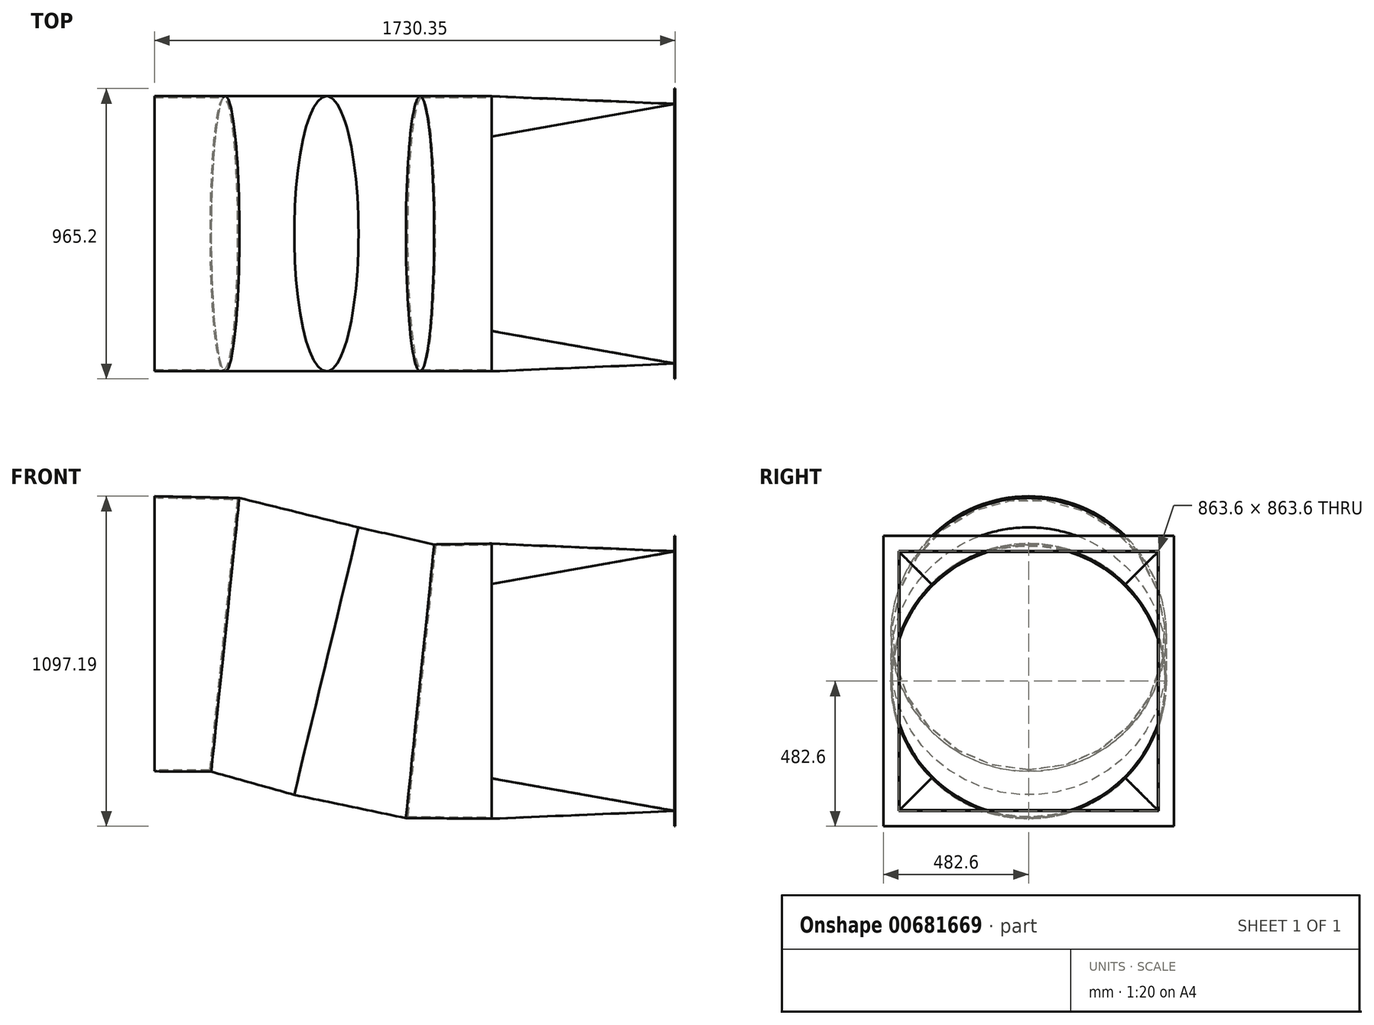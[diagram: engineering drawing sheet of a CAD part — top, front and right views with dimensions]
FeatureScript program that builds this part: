
annotation { "Feature Type Name" : "Feature", "Feature Type Description" : "" }
export const myFeature = defineFeature(function(context is Context, id is Id, definition is map)
    precondition{}
    {
        {
            var Q0;
            Q0=qCreatedBy(makeId("Right.planeOp"),FACE);
            var sketch = newSketch(context, id + "F0", { "sketchPlane" : qUnion([Q0])});
            skLineSegment(sketch, "E0.bottom", {"start": v(482.6, 482.6) * mm, "end": v(-482.6, 482.6) * mm});
            skLineSegment(sketch, "E0.top", {"start": v(482.6, -482.6) * mm, "end": v(-482.6, -482.6) * mm});
            skLineSegment(sketch, "E0.left", {"start": v(482.6, 482.6) * mm, "end": v(482.6, -482.6) * mm});
            skLineSegment(sketch, "E0.right", {"start": v(-482.6, 482.6) * mm, "end": v(-482.6, -482.6) * mm});
            skPoint(sketch, "E0.middle", {"position": v(0, 0) * mm});
            skCircle(sketch, "E1", {"center": v(0, 0) * mm, "radius": 431.8 * mm});
            skLineSegment(sketch, "E2.bottom", {"start": v(431.8, 431.8) * mm, "end": v(-431.8, 431.8) * mm});
            skLineSegment(sketch, "E2.top", {"start": v(431.8, -431.8) * mm, "end": v(-431.8, -431.8) * mm});
            skLineSegment(sketch, "E2.left", {"start": v(431.8, 431.8) * mm, "end": v(431.8, -431.8) * mm});
            skLineSegment(sketch, "E2.right", {"start": v(-431.8, 431.8) * mm, "end": v(-431.8, -431.8) * mm});
            skSolve(sketch);
        }
        {
            var Q0;
            Q0=makeQuery(id+"F0.imprint","IMPRINT",FACE,{"disambiguationData":[TD([[makeQuery(id+"F0.imprint","IMPRINT",EDGE,{"derivedFrom":sQuery(id+"F0.wireOp",EDGE,"E0.bottom")}),1.0]])]});
            extrude(context, id + "F1", {"entities" : qUnion([Q0]), "oppositeDirection" : true, "depth" : 3.17 * mm, "offsetDistance" : 25.4 * mm});
        }
        {
            var Q0;
            {var subQ0=sQuery(id+"F0.wireOp",EDGE,"E1");var subQ1=makeQuery(id+"F0.imprint","INTERSECT",VERTEX,{"derivedFrom":[subQ0,sQuery(id+"F0.wireOp",EDGE,"E2.bottom")]});Q0=makeQuery(id+"F0.imprint","IMPRINT",FACE,{"disambiguationData":[TD([[makeQuery(id+"F0.imprint","IMPRINT",EDGE,{"disambiguationData":[TD([[subQ1,1.0]])],"derivedFrom":subQ0}),1.0]])]});}
            cPlane(context, id + "F2", {"entities" : qUnion([Q0]), "cplaneType" : CPlaneType.OFFSET, "offset" : 609.6 * mm, "oppositeDirection" : true, "width" : 152.4 * mm, "height" : 152.4 * mm});
        }
        {
            var Q0;
            Q0=qCreatedBy(id+"F2.planeOp",FACE);
            var sketch = newSketch(context, id + "F3", { "sketchPlane" : qUnion([Q0])});
            skCircle(sketch, "E3", {"center": v(0, 0) * mm, "radius": 457.2 * mm});
            skSolve(sketch);
        }
        {
            var Q0;
            Q0=qCreatedBy(makeId("Right.planeOp"),FACE);
            var sketch = newSketch(context, id + "F4", { "sketchPlane" : qUnion([Q0])});
            skLineSegment(sketch, "E4.bottom", {"start": v(431.8, 431.8) * mm, "end": v(-431.8, 431.8) * mm});
            skLineSegment(sketch, "E4.top", {"start": v(431.8, -431.8) * mm, "end": v(-431.8, -431.8) * mm});
            skLineSegment(sketch, "E4.left", {"start": v(431.8, 431.8) * mm, "end": v(431.8, -431.8) * mm});
            skLineSegment(sketch, "E4.right", {"start": v(-431.8, 431.8) * mm, "end": v(-431.8, -431.8) * mm});
            skSolve(sketch);
        }
        {
            var Q1;
            Q1=makeQuery(id+"F3.imprint","IMPRINT",FACE,{"disambiguationData":[TD([[makeQuery(id+"F3.imprint","IMPRINT",EDGE,{"derivedFrom":sQuery(id+"F3.wireOp",EDGE,"E3")}),1.0]])]});
            var Q2;
            Q2=makeQuery(id+"F4.imprint","IMPRINT",FACE,{"disambiguationData":[TD([[makeQuery(id+"F4.imprint","IMPRINT",EDGE,{"derivedFrom":sQuery(id+"F4.wireOp",EDGE,"E4.bottom")}),1.0]])]});
            loft(context, id + "F5", {"sheetProfilesArray" : [{ "sheetProfileEntities" : qUnion([Q1]) }, { "sheetProfileEntities" : qUnion([Q2]) }]});
        }
        {
            var Q0;
            Q0=makeQuery(id+"F5.opLoft","CAP_FACE",FACE,{"disambiguationData":[OSD([makeQuery(id+"F3.imprint","IMPRINT",FACE,{"disambiguationData":[TD([[makeQuery(id+"F3.imprint","IMPRINT",EDGE,{"derivedFrom":sQuery(id+"F3.wireOp",EDGE,"E3")}),1.0]])]})])],"isStart":true});
            var Q1;
            Q1=makeQuery(id+"F5.opLoft","CAP_FACE",FACE,{"disambiguationData":[OSD([makeQuery(id+"F4.imprint","IMPRINT",FACE,{"disambiguationData":[TD([[makeQuery(id+"F4.imprint","IMPRINT",EDGE,{"derivedFrom":sQuery(id+"F4.wireOp",EDGE,"E4.bottom")}),1.0]])]})])],"isStart":true});
            shell(context, id + "F6", {"entities" : qUnion([Q0, Q1]), "thickness" : 2.54 * mm});
        }
        {
            var Q0;
            Q0=qCreatedBy(makeId("Front.planeOp"),FACE);
            var sketch = newSketch(context, id + "F7", { "sketchPlane" : qUnion([Q0])});
            skLineSegment(sketch, "E5", {"start": v(-611.03, 0) * mm, "end": v(-2931.64, 0) * mm, "construction": true});
            skLineSegment(sketch, "E6.bottom", {"start": v(-612.75, 435.19) * mm, "end": v(-1730.35, 435.19) * mm});
            skLineSegment(sketch, "E6.top", {"start": v(-612.75, -428.41) * mm, "end": v(-1730.35, -428.41) * mm});
            skLineSegment(sketch, "E6.left", {"start": v(-612.75, 435.19) * mm, "end": v(-612.75, -428.41) * mm});
            skLineSegment(sketch, "E6.right", {"start": v(-1730.35, 435.19) * mm, "end": v(-1730.35, -428.41) * mm});
            skLineSegment(sketch, "E7.bottom", {"start": v(-612.75, 435.19) * mm, "end": v(-1729.64, 435.19) * mm});
            skLineSegment(sketch, "E7.top", {"start": v(-612.75, 590.76) * mm, "end": v(-1729.64, 590.76) * mm});
            skLineSegment(sketch, "E7.left", {"start": v(-612.75, 435.19) * mm, "end": v(-612.75, 590.76) * mm});
            skLineSegment(sketch, "E7.right", {"start": v(-1729.64, 435.19) * mm, "end": v(-1729.64, 590.76) * mm});
            skLineSegment(sketch, "E8.bottom", {"start": v(-612.75, 435.19) * mm, "end": v(-803.25, 435.19) * mm});
            skLineSegment(sketch, "E8.top", {"start": v(-612.75, -428.41) * mm, "end": v(-803.25, -428.41) * mm});
            skLineSegment(sketch, "E9.bottom", {"start": v(-1729.64, 590.76) * mm, "end": v(-1450.24, 590.76) * mm});
            skLineSegment(sketch, "E9.top", {"start": v(-1729.64, -272.84) * mm, "end": v(-1539.14, -272.84) * mm});
            skLineSegment(sketch, "E9.left", {"start": v(-1729.64, 590.76) * mm, "end": v(-1729.64, -272.84) * mm});
            skLineSegment(sketch, "E10", {"start": v(-803.25, 435.19) * mm, "end": v(-1450.24, 590.76) * mm});
            skLineSegment(sketch, "E11.bottom", {"start": v(-612.75, -428.41) * mm, "end": v(-892.15, -428.41) * mm});
            skLineSegment(sketch, "E11.left", {"start": v(-612.75, -428.41) * mm, "end": v(-612.75, -156.4) * mm});
            skLineSegment(sketch, "E12.left", {"start": v(-1729.64, -272.84) * mm, "end": v(-1729.64, -35.15) * mm});
            skLineSegment(sketch, "E13", {"start": v(-892.15, -428.41) * mm, "end": v(-1539.14, -272.84) * mm});
            skLineSegment(sketch, "E14.bottom", {"start": v(-1450.24, 590.76) * mm, "end": v(-1056.12, 590.76) * mm});
            skLineSegment(sketch, "E15", {"start": v(-1056.12, 495.99) * mm, "end": v(-1257.29, -340.61) * mm});
            skLineSegment(sketch, "E16", {"start": v(-1450.24, 590.76) * mm, "end": v(-1539.14, -272.84) * mm});
            skLineSegment(sketch, "E17", {"start": v(-803.25, 435.19) * mm, "end": v(-892.15, -428.41) * mm});
            skLineSegment(sketch, "E18", {"start": v(-848.05, 0) * mm, "end": v(-1156.7, 77.69) * mm, "construction": true});
            skLineSegment(sketch, "E19", {"start": v(-1156.7, 77.69) * mm, "end": v(-1494.7, 158.96) * mm, "construction": true});
            skLineSegment(sketch, "E20", {"start": v(-1494.7, 158.96) * mm, "end": v(-1730.35, 158.96) * mm, "construction": true});
            skSolve(sketch);
        }
        {
            var Q0;
            Q0=sQuery(id+"F7.wireOp",EDGE,"E17");
            cPlane(context, id + "F8", {"entities" : qUnion([Q0]), "cplaneType" : CPlaneType.LINE_ANGLE, "offset" : 25.4 * mm, "angle" : 0 * degree, "width" : 152.4 * mm, "height" : 152.4 * mm});
        }
        {
            var Q0;
            Q0=sQuery(id+"F7.wireOp",EDGE,"E15");
            cPlane(context, id + "F9", {"entities" : qUnion([Q0]), "cplaneType" : CPlaneType.LINE_ANGLE, "offset" : 25.4 * mm, "angle" : 0 * degree, "width" : 152.4 * mm, "height" : 152.4 * mm});
        }
        {
            var Q0;
            Q0=sQuery(id+"F7.wireOp",EDGE,"E16");
            cPlane(context, id + "F10", {"entities" : qUnion([Q0]), "cplaneType" : CPlaneType.LINE_ANGLE, "offset" : 25.4 * mm, "angle" : 0 * degree, "width" : 152.4 * mm, "height" : 152.4 * mm});
        }
        {
            var Q0;
            Q0=sQuery(id+"F7.wireOp",EDGE,"E6.right");
            cPlane(context, id + "F11", {"entities" : qUnion([Q0]), "cplaneType" : CPlaneType.LINE_ANGLE, "offset" : 25.4 * mm, "angle" : 0 * degree, "width" : 152.4 * mm, "height" : 152.4 * mm});
        }
        {
            var Q0;
            Q0=qCreatedBy(id+"F9.planeOp",FACE);
            var sketch = newSketch(context, id + "F12", { "sketchPlane" : qUnion([Q0])});
            skCircle(sketch, "E21", {"center": v(0, -206.28) * mm, "radius": 457.2 * mm});
            skSolve(sketch);
        }
        {
            var Q0;
            Q0=qCreatedBy(id+"F10.planeOp",FACE);
            var sketch = newSketch(context, id + "F13", { "sketchPlane" : qUnion([Q0])});
            skCircle(sketch, "E22", {"center": v(0, 0) * mm, "radius": 457.2 * mm});
            skSolve(sketch);
        }
        {
            var Q0;
            Q0=qCreatedBy(id+"F8.planeOp",FACE);
            var sketch = newSketch(context, id + "F14", { "sketchPlane" : qUnion([Q0])});
            skCircle(sketch, "E23", {"center": v(0, -87.24) * mm, "radius": 457.2 * mm});
            skSolve(sketch);
        }
        {
            var Q0;
            Q0=qCreatedBy(id+"F2.planeOp",FACE);
            var sketch = newSketch(context, id + "F15", { "sketchPlane" : qUnion([Q0])});
            skCircle(sketch, "E24", {"center": v(0, 0) * mm, "radius": 457.2 * mm});
            skSolve(sketch);
        }
        {
            var Q0;
            Q0=makeQuery(id+"F15.imprint","IMPRINT",FACE,{"disambiguationData":[TD([[makeQuery(id+"F15.imprint","IMPRINT",EDGE,{"derivedFrom":sQuery(id+"F15.wireOp",EDGE,"E24")}),1.0]])]});
            var Q1;
            Q1=makeQuery(id+"F14.imprint","IMPRINT",FACE,{"disambiguationData":[TD([[makeQuery(id+"F14.imprint","IMPRINT",EDGE,{"derivedFrom":sQuery(id+"F14.wireOp",EDGE,"E23")}),1.0]])]});
            loft(context, id + "F16", {"sheetProfilesArray" : [{ "sheetProfileEntities" : qUnion([Q0]) }, { "sheetProfileEntities" : qUnion([Q1]) }]});
        }
        {
            var Q0;
            Q0=makeQuery(id+"F14.imprint","IMPRINT",FACE,{"disambiguationData":[TD([[makeQuery(id+"F14.imprint","IMPRINT",EDGE,{"derivedFrom":sQuery(id+"F14.wireOp",EDGE,"E23")}),1.0]])]});
            var Q1;
            Q1=makeQuery(id+"F12.imprint","IMPRINT",FACE,{"disambiguationData":[TD([[makeQuery(id+"F12.imprint","IMPRINT",EDGE,{"derivedFrom":sQuery(id+"F12.wireOp",EDGE,"E21")}),1.0]])]});
            loft(context, id + "F17", {"sheetProfilesArray" : [{ "sheetProfileEntities" : qUnion([Q0]) }, { "sheetProfileEntities" : qUnion([Q1]) }]});
        }
        {
            var Q0;
            Q0=qCreatedBy(id+"F11.planeOp",FACE);
            var sketch = newSketch(context, id + "F18", { "sketchPlane" : qUnion([Q0])});
            skCircle(sketch, "E25", {"center": v(0, 157.4) * mm, "radius": 457.2 * mm});
            skSolve(sketch);
        }
        {
            var Q0;
            Q0=makeQuery(id+"F12.imprint","IMPRINT",FACE,{"disambiguationData":[TD([[makeQuery(id+"F12.imprint","IMPRINT",EDGE,{"derivedFrom":sQuery(id+"F12.wireOp",EDGE,"E21")}),1.0]])]});
            var Q1;
            Q1=makeQuery(id+"F13.imprint","IMPRINT",FACE,{"disambiguationData":[TD([[makeQuery(id+"F13.imprint","IMPRINT",EDGE,{"derivedFrom":sQuery(id+"F13.wireOp",EDGE,"E22")}),1.0]])]});
            loft(context, id + "F19", {"sheetProfilesArray" : [{ "sheetProfileEntities" : qUnion([Q0]) }, { "sheetProfileEntities" : qUnion([Q1]) }]});
        }
        {
            var Q0;
            Q0=makeQuery(id+"F13.imprint","IMPRINT",FACE,{"disambiguationData":[TD([[makeQuery(id+"F13.imprint","IMPRINT",EDGE,{"derivedFrom":sQuery(id+"F13.wireOp",EDGE,"E22")}),1.0]])]});
            var Q1;
            Q1=makeQuery(id+"F18.imprint","IMPRINT",FACE,{"disambiguationData":[TD([[makeQuery(id+"F18.imprint","IMPRINT",EDGE,{"derivedFrom":sQuery(id+"F18.wireOp",EDGE,"E25")}),1.0]])]});
            loft(context, id + "F20", {"sheetProfilesArray" : [{ "sheetProfileEntities" : qUnion([Q0]) }, { "sheetProfileEntities" : qUnion([Q1]) }]});
        }
        {
            var Q0;
            Q0=makeQuery(id+"F20.opLoft","CAP_FACE",FACE,{"disambiguationData":[OSD([makeQuery(id+"F18.imprint","IMPRINT",FACE,{"disambiguationData":[TD([[makeQuery(id+"F18.imprint","IMPRINT",EDGE,{"derivedFrom":sQuery(id+"F18.wireOp",EDGE,"E25")}),1.0]])]})])],"isStart":true});
            var Q1;
            Q1=makeQuery(id+"F16.opLoft","CAP_FACE",FACE,{"disambiguationData":[OSD([makeQuery(id+"F15.imprint","IMPRINT",FACE,{"disambiguationData":[TD([[makeQuery(id+"F15.imprint","IMPRINT",EDGE,{"derivedFrom":sQuery(id+"F15.wireOp",EDGE,"E24")}),1.0]])]})])],"isStart":true});
            shell(context, id + "F21", {"entities" : qUnion([Q0, Q1]), "thickness" : 5.08 * mm});
        }
    });
